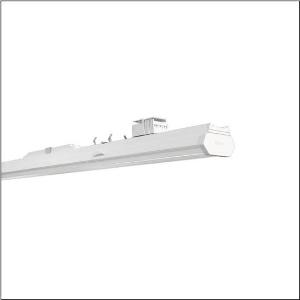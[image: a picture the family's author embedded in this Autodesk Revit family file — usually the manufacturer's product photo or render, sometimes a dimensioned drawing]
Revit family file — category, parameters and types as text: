
# Revit family: licross_r__21_protected_mo_52td12dn4a5gd_b3fc
name_source: partatom
category: Lighting Fixtures
units: mm (PartAtom-declared; Revit-internal decimal feet)

## family parameters
Cut with Voids When Loaded = No
Host = Face
Light Source = No
Part Type = Normal
Room Calculation Point = No
Round Connector Dimension = Use Diameter
Shared = No

## types (1)
- --- (1 x LED, 1610 lm, 10.2 W, 4000K)
    Apparent Load = 10 VA
    CIE Flux Codes = 73 92 98 99 100
    Color Rendering = 80
    Color Temperature = 4000K
    Default Elevation = 1800 mm
    Description = Licross® 21 Protected MO, luminaire insert, of sheet steel, galvanised, coil coated, white, length: 1.500mm, width: 90mm, height: 103mm, LED rated luminous flux: 10.700lm, light colour: 840, control gear: DALI 2, with plug, 6-pole, with phase selection, mains connection: 220..240V, AC/DC, 0/50..60Hz, rated input power: 62W, without changeover relay, for emergency light function, for central battery installations according to DIN EN 60598-2-22, halogen-free wiring, primary light control with lens, of plastic, primary optical cover: cover, of PMMA, light emission: direct distribution, primary light characteristic: symmetric, protection rating (complete): IP54, insulation class (complete): insulation class I (protective earthing), certification: CE, ENEC, VDE, UKCA, protection symbol: D if used in an environment with non-conductive dust loads with corresponding accessories, impact resistance: IK06, permissible ambient temperature for indoor applications: -25..+35°C, standard: EN 60598-2-22, corresponds to IFS (International Featured Standards) requirements for safety and quality in the food industry, reducing of maximum allowable ambient temperature of 5°C with ceiling mounting, LABS conformity tested according to VDMA 24364:2018-05, packaging unit: 1 piece
    Height = 92 mm
    Lamp = 1 x LED
    Lamp Light Flux = 1610 lm
    Lamp Power = 10.2 W
    Lamp count = 1
    Length = 1500 mm
    Luminous efficacy = 158 lm/W
    Manufacturer = Siteco
    ModVariant = No
    Model = 52TD12DN4A5GD
    Mounting Place = Ceiling
    Mounting Type = Pendant
    Number of Poles = 1
    OnlyDefault = Yes
    Power Factor = 1
    Product Name = Licross® 21 Protected MO
    Product group = luminaire insert
    ProductGroupID = 901
    Protection Class = Protection class I
    Protection Degree = IP 54
    RLX_Detail_Level = 1
    RLX_Emergency_Light_Flux = 0 lm
    RLX_Emergency_Type = 0
    RLX_Emergency_Type_DB = No
    RlxData = <blob elided: 24909 chars, md5=95517d88>
    Socket = socket
    Standby Power = 0 W
    System Light Flux = 1610 lm
    System Power = 10 W
    Type Comments = : DC mode (central or group accumulator) initial emergency light level
    Type Image = l_1256148.jpg
    URL = http://relux.com
    VarID = @adj_046299
    Voltage = 0 V
    Weight = 0.00 kg
    Width = 88 mm

## geometry (parser evidence)
native form markers: Blend x4, Sweep x8
no freeform markers — native parametric forms only
